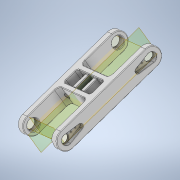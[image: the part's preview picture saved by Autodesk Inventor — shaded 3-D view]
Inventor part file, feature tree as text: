
AUTODESK INVENTOR PART (.ipt)
format: ipt  version: 2020.3 (Build 243373000, 373)  size: 617,472 bytes
history: native  units: mm
features: fillet x14, sketch x9, extrude x8, plane x5, hole x3, chamfer x2
ambient origin geometry x8: Origin, YZ Plane, XZ Plane, XY Plane, X Axis, Y Axis, Z Axis, Center Point
bodies: Solid1 (feature_tree)
feature tree (41):
  extrude  "Extrusion1"  Depth=34.5mm
  sketch  "Sketch2"  dims[d11=20.0mm d12=15.0mm d13=0.0mm d14=3.0mm d15=6.0mm d16=4.0mm d19=6.0mm d20=0.0mm]
  extrude  "Extrusion2"  Depth=15.0mm TaperAngle=0.0deg
  fillet  "Fillet1"  Radius=3.0mm
  fillet  "Fillet2"  Radius=6.0mm
  fillet  "Fillet3"  Radius=4.0mm
  fillet  "Fillet4"  Radius=6.0mm
  sketch  "Sketch5"  dims[d30=35.0mm d31=35.0mm]
  extrude  "Extrusion4"  Depth=35.0mm
  extrude  "Extrusion5"  Depth=12.1mm
  hole  "Hole7"  [1 undecoded]
  extrude  "Extrusion6"  Depth=1.0mm TaperAngle=0.0deg
  extrude  "Extrusion7"  Depth=12.1mm
  hole  "Hole5"  [1 undecoded]
  fillet  "Fillet13"  Radius=0.5mm
  fillet  "Fillet11"  Radius=2.0mm
  fillet  "Fillet9"  Radius=0.2mm
  fillet  "Fillet15"  Radius=3.5mm
  fillet  "Fillet12"  Radius=0.5mm
  hole  "Hole6"  [1 undecoded]
  fillet  "Fillet14"  Radius=0.5mm
  fillet  "Fillet16"  Radius=0.3mm
  fillet  "Fillet17"  Radius=2.0mm
  plane  "Work Plane1"
  plane  "Work Plane2"
  extrude  "Extrusion8"  Depth=2.0mm
  extrude  "Extrusion9"  Depth=2.0mm
  chamfer  "Chamfer1"  Distance=35.0mm
  chamfer  "Chamfer2"  Distance=7.0mm
  fillet  "Fillet20"  Radius=7.0mm
  fillet  "Fillet21"  Radius=0.2mm
  plane  "Work Plane4"
  plane  "Work Plane5"
  plane  "Work Plane6"
  sketch  "Sketch1"  dims[d2=6.0mm d8=34.5mm]
  sketch  "Sketch6"  dims[d53=3.7mm d54=12.1mm]
  sketch  "Sketch12"  dims[d61=4.0mm d62=0.0mm d63=3.5mm d64=0.0mm]
  sketch  "Sketch13"  dims[d68=1.0mm d69=0.0mm d70=1.0mm d71=0.0mm]
  sketch  "Sketch14"  dims[d72=1.0mm d76=12.1mm]
  sketch  "Sketch15"  dims[d89=7.2mm d97=3.5mm]
  sketch  "Sketch16"  dims[d98=4.0mm d99=6.0mm d100=4.0mm d101=2.0mm d102=90.0deg d103=5.0mm d104=20.594885mm d105=0.5mm d107=2.0mm d108=0.2mm d109=3.5mm d110=8.8mm d111=6.0mm d112=4.0mm d113=2.0mm d114=90.0deg d115=5.0mm d116=20.594885mm d117=0.5mm d118=0.5mm d119=0.5mm d120=0.3mm d121=2.0mm d122=2.0mm d123=2.0mm d124=1.0mm d125=6.0mm d126=4.0mm d127=2.0mm d128=90.0deg d129=10.0mm d130=20.594885mm d131=35.0mm d132=7.0mm d133=7.0mm d134=0.0mm d138=0.2mm d139=0.8mm d140=45.0deg d141=1.0mm d142=2.0mm d143=-90.0mm d144=7.0mm d145=0.0mm d146=0.2mm d147=0.8mm d148=45.0deg d149=-7.5mm d150=-23.25mm d151=7.5mm]
note: 3 required parameter values undecoded (feature->parameter linkage not recoverable at this tier; creation-order binding heuristic only, values carry confidence <= 0.55)
